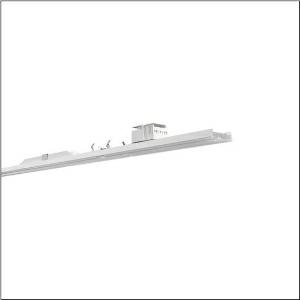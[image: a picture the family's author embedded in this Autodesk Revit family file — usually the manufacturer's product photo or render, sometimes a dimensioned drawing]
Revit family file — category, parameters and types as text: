
# Revit family: licross_r__11_recessed_ho_51tl11dn4dxr_2cb6
name_source: partatom
category: Lighting Fixtures
units: mm (PartAtom-declared; Revit-internal decimal feet)

## family parameters
Cut with Voids When Loaded = No
Host = Face
Light Source = No
Part Type = Normal
Room Calculation Point = No
Round Connector Dimension = Use Diameter
Shared = No

## types (1)
- --- (1 x LED, 13060 lm, 76.5 W, 4000K)
    Apparent Load = 77 VA
    CIE Flux Codes = 87 95 99 100 100
    Color Rendering = 80
    Color Temperature = 4000K
    Default Elevation = 1800 mm
    Description = Licross® 11 Recessed HOluminaire insert, length: 1.500mm, width: 66mm, height: 67mm, LED rated luminous flux: 13.060lm, light colour: 840, control gear: DALI 2, control gear: ECG DALI, with plug, 5-pole, with phase selection, mains connection: 220..240V, AC, 50/60Hz, halogen-free wiring, primary optical cover: cover, of PMMA, light emission: direct distribution, protection rating (complete): IP40, insulation class (complete): insulation class I (protective earthing), certification: CE, ENEC, VDE, protection symbol: D if used in an environment without relevant dust loads with corresponding accessories, permissible ambient temperature for indoor applications: -25..+30°C, reducing of maximum allowable ambient temperature of 5°C with ceiling mounting, corresponds to IFS (International Featured Standards) requirements for safety and quality in the food industry, packaging unit: 1 piece
    Height = 58 mm
    Lamp = 1 x LED
    Lamp Light Flux = 13060 lm
    Lamp Power = 76.5 W
    Lamp count = 1
    Length = 1500 mm
    Luminous efficacy = 171 lm/W
    Manufacturer = Siteco
    ModVariant = No
    Model = 51TL11DN4DXR
    Mounting Place = Ceiling
    Mounting Type = Pendant
    Number of Poles = 1
    OnlyDefault = Yes
    Power Factor = 1
    Product Name = Licross® 11 Recessed HO
    Product group = luminaire insert
    ProductGroupID = 902
    Protection Class = Protection class I
    Protection Degree = IP 40
    RLX_Detail_Level = 1
    RlxData = <blob elided: 22165 chars, md5=cec49804>
    Socket = socket
    Standby Power = 0 W
    System Light Flux = 13060 lm
    System Power = 77 W
    Type Comments = factory setting: luminous flux: 100 % | dim-lin: 254 | 435 mA
    Type Image = l_1266722.jpg
    URL = http://relux.com
    VarID = @adj_138789
    Voltage = 0 V
    Weight = 0.00 kg
    Width = 66 mm

## geometry (parser evidence)
native form markers: Blend x4, Sweep x12
no freeform markers — native parametric forms only
